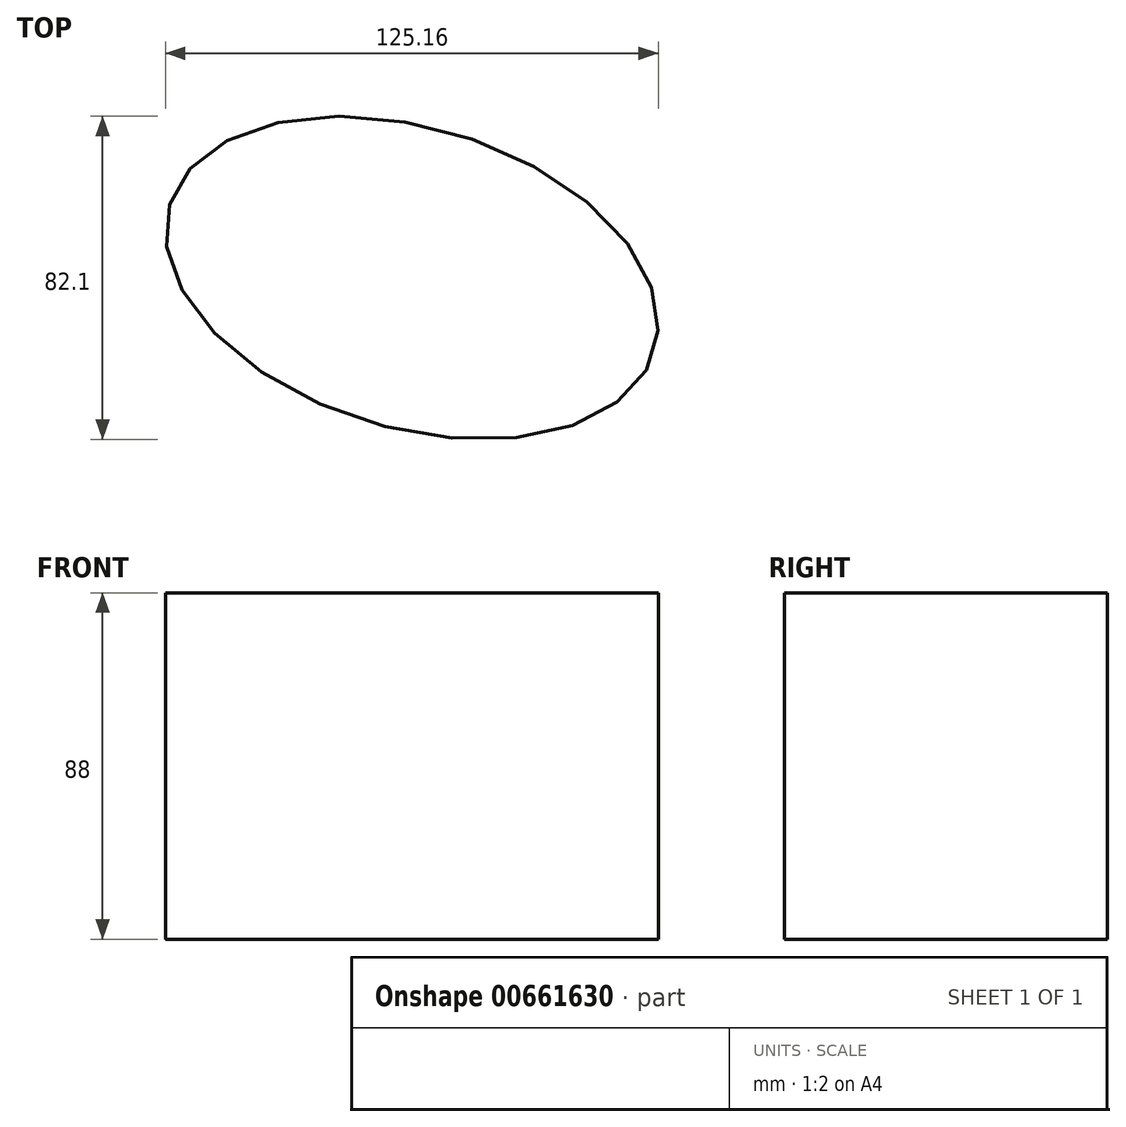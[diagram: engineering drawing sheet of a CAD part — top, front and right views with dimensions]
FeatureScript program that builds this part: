
annotation { "Feature Type Name" : "Feature", "Feature Type Description" : "" }
export const myFeature = defineFeature(function(context is Context, id is Id, definition is map)
    precondition{}
    {
        {
            var Q0;
            Q0=qCreatedBy(makeId("Top.planeOp"),FACE);
            var sketch = newSketch(context, id + "F0", { "sketchPlane" : qUnion([Q0])});
            skEllipse(sketch, "E0", {"center": v(0, 0) * mm, "majorRadius": 64.34 * mm, "minorRadius": 38.24 * mm, "majorAxis": v(-0.96, 0.29)});
            skSolve(sketch);
        }
        {
            var Q0;
            Q0=makeQuery(id+"F0.imprint","IMPRINT",FACE,{"disambiguationData":[TD([[makeQuery(id+"F0.imprint","IMPRINT",EDGE,{"derivedFrom":sQuery(id+"F0.wireOp",EDGE,"E0")}),1.0]])]});
            extrude(context, id + "F1", {"entities" : qUnion([Q0]), "depth" : 88 * mm, "offsetDistance" : 25 * mm});
        }
    });
